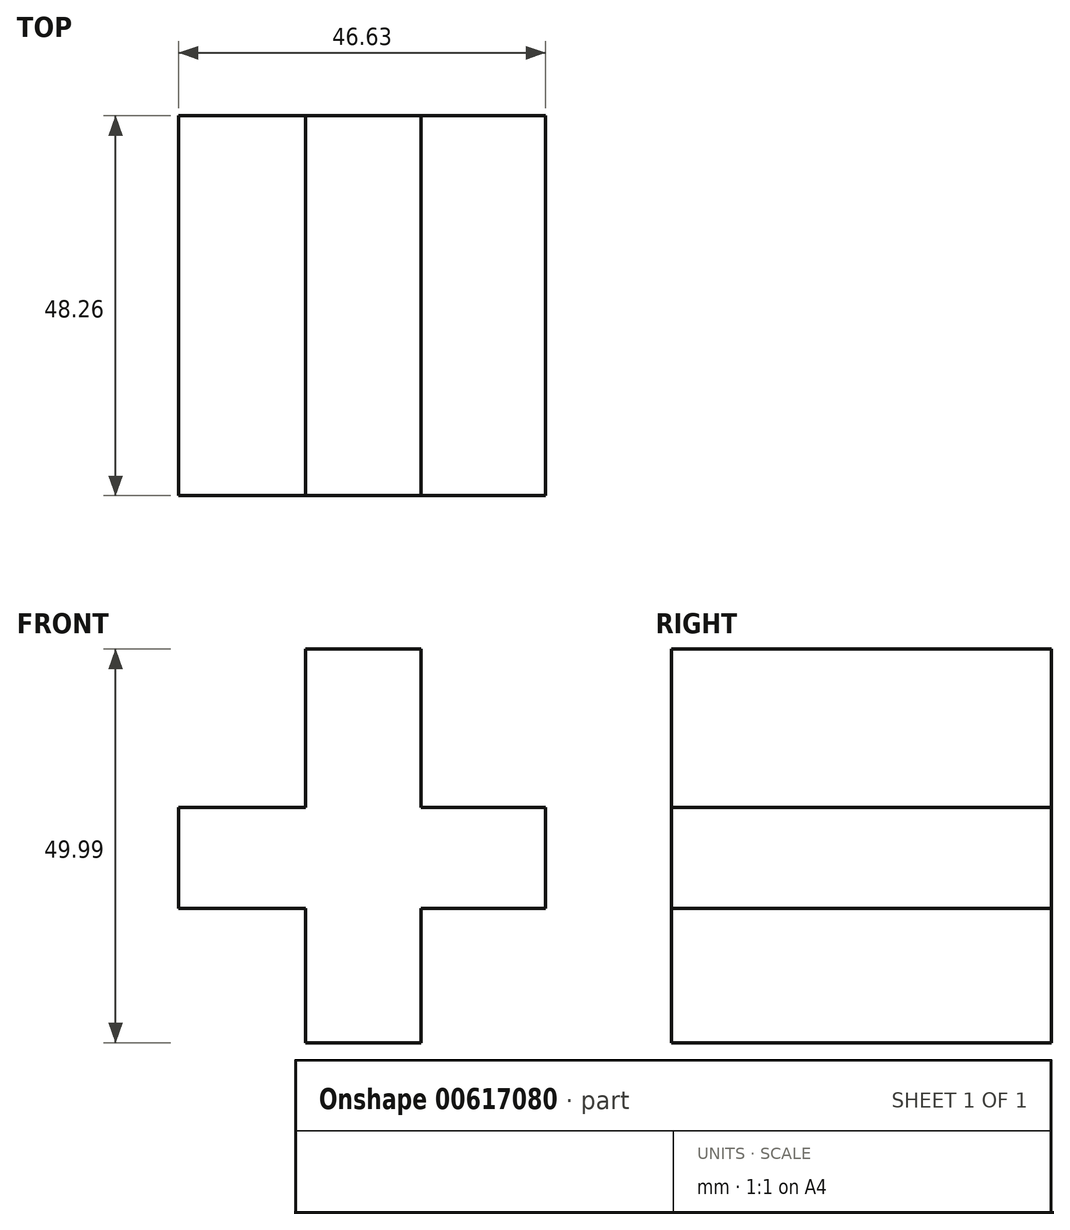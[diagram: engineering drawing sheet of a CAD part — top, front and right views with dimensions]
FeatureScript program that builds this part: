
annotation { "Feature Type Name" : "Feature", "Feature Type Description" : "" }
export const myFeature = defineFeature(function(context is Context, id is Id, definition is map)
    precondition{}
    {
        {
            var Q0;
            Q0=qCreatedBy(makeId("Front.planeOp"),FACE);
            var sketch = newSketch(context, id + "F0", { "sketchPlane" : qUnion([Q0])});
            skLineSegment(sketch, "E0", {"start": v(-24.54, 0) * mm, "end": v(-24.54, 20.12) * mm});
            skLineSegment(sketch, "E1", {"start": v(-24.54, 20.12) * mm, "end": v(-9.9, 20.12) * mm});
            skLineSegment(sketch, "E2", {"start": v(-9.9, 20.12) * mm, "end": v(-9.9, 0) * mm});
            skLineSegment(sketch, "E3", {"start": v(-9.9, 0) * mm, "end": v(5.94, 0) * mm});
            skLineSegment(sketch, "E4", {"start": v(5.94, 0) * mm, "end": v(5.94, -12.8) * mm});
            skLineSegment(sketch, "E5", {"start": v(5.94, -12.8) * mm, "end": v(-9.9, -12.8) * mm});
            skLineSegment(sketch, "E6", {"start": v(-9.9, -12.8) * mm, "end": v(-9.9, -29.87) * mm});
            skLineSegment(sketch, "E7", {"start": v(-9.9, -29.87) * mm, "end": v(-24.54, -29.87) * mm});
            skLineSegment(sketch, "E8", {"start": v(-24.54, -29.87) * mm, "end": v(-24.54, -12.8) * mm});
            skLineSegment(sketch, "E9", {"start": v(-24.54, -12.8) * mm, "end": v(-40.7, -12.8) * mm});
            skLineSegment(sketch, "E10", {"start": v(-40.7, -12.8) * mm, "end": v(-40.7, 0) * mm});
            skLineSegment(sketch, "E11", {"start": v(-40.7, 0) * mm, "end": v(-24.54, 0) * mm});
            skSolve(sketch);
        }
        {
            var Q0;
            Q0 = qSketchRegion(id + "F0", true);
            extrude(context, id + "F1", {"entities" : qUnion([Q0]), "depth" : 48.26 * mm, "offsetDistance" : 25.4 * mm});
        }
    });
